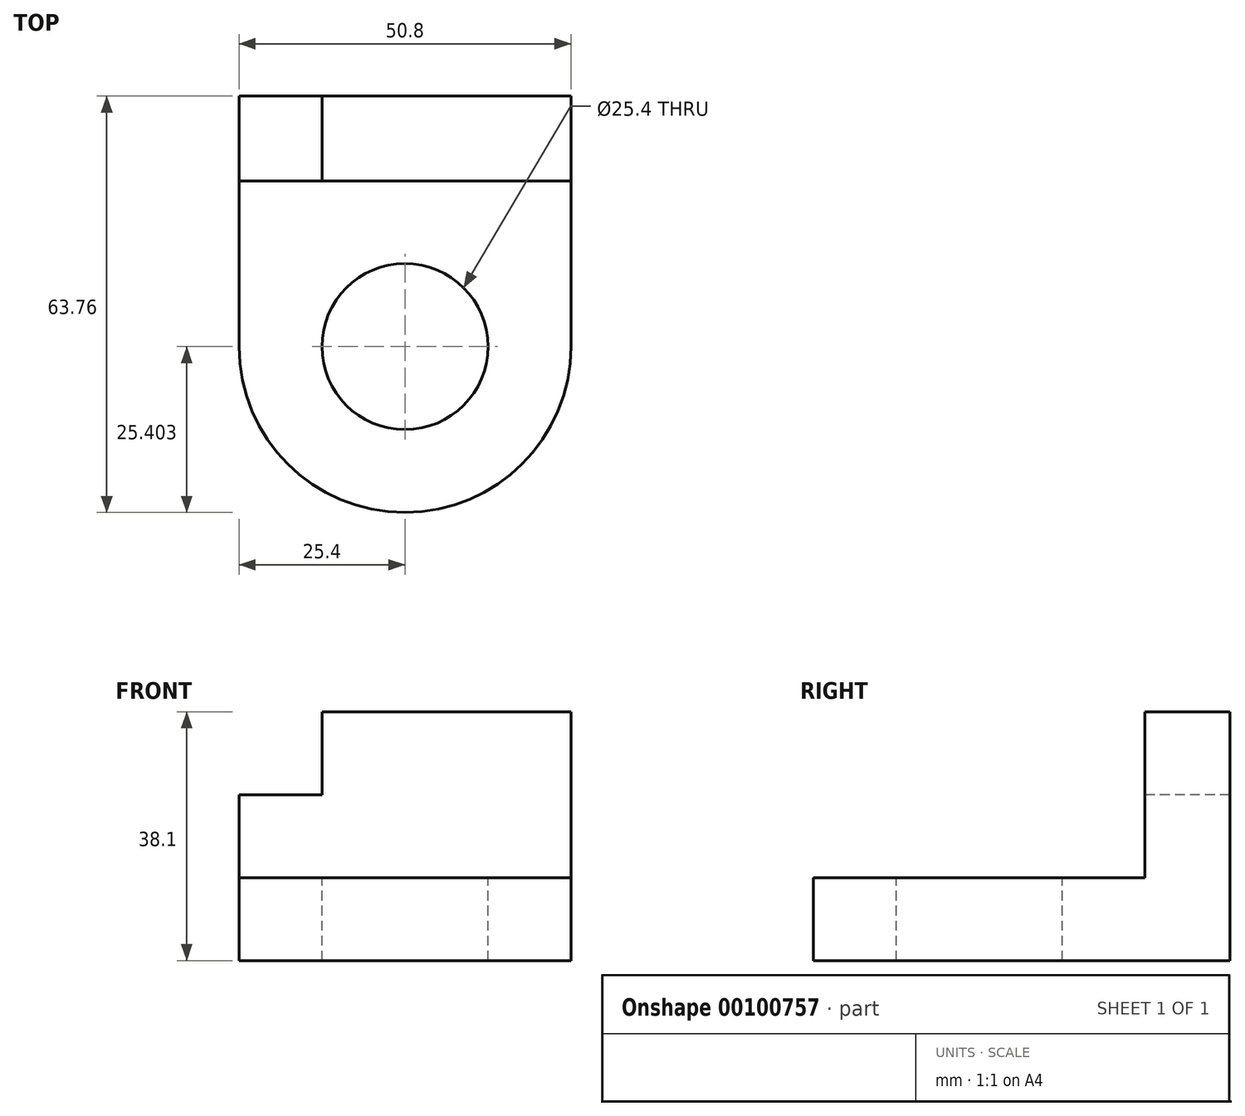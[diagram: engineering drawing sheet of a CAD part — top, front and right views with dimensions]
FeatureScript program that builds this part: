
annotation { "Feature Type Name" : "Feature", "Feature Type Description" : "" }
export const myFeature = defineFeature(function(context is Context, id is Id, definition is map)
    precondition{}
    {
        {
            var Q0;
            Q0=qCreatedBy(makeId("Top.planeOp"),FACE);
            var sketch = newSketch(context, id + "F0", { "sketchPlane" : qUnion([Q0])});
            skLineSegment(sketch, "E0.bottom", {"start": v(-25.4, 31.88) * mm, "end": v(25.4, 31.88) * mm});
            skLineSegment(sketch, "E0.top", {"start": v(-25.4, -31.88) * mm, "end": v(25.4, -31.88) * mm});
            skLineSegment(sketch, "E0.left", {"start": v(-25.4, 31.88) * mm, "end": v(-25.4, -31.88) * mm});
            skLineSegment(sketch, "E0.right", {"start": v(25.4, 31.88) * mm, "end": v(25.4, -31.88) * mm});
            skPoint(sketch, "E0.middle", {"position": v(0, 0) * mm});
            skSolve(sketch);
        }
        {
            var Q0;
            Q0=makeQuery(id+"F0.imprint","IMPRINT",FACE,{"disambiguationData":[TD([[makeQuery(id+"F0.imprint","IMPRINT",EDGE,{"derivedFrom":sQuery(id+"F0.wireOp",EDGE,"E0.bottom")}),-1.0]])]});
            extrude(context, id + "F1", {"entities" : qUnion([Q0]), "depth" : 12.7 * mm});
        }
        {
            var Q0;
            Q0=qCreatedBy(makeId("Top.planeOp"),FACE);
            var sketch = newSketch(context, id + "F2", { "sketchPlane" : qUnion([Q0])});
            skLineSegment(sketch, "E1.bottom", {"start": v(-25.4, 31.88) * mm, "end": v(25.4, 31.88) * mm});
            skLineSegment(sketch, "E1.top", {"start": v(-25.4, 18.85) * mm, "end": v(25.4, 18.85) * mm});
            skLineSegment(sketch, "E1.left", {"start": v(-25.4, 31.88) * mm, "end": v(-25.4, 18.85) * mm});
            skLineSegment(sketch, "E1.right", {"start": v(25.4, 31.88) * mm, "end": v(25.4, 18.85) * mm});
            skSolve(sketch);
        }
        {
            var Q0;
            Q0 = qSketchRegion(id + "F2", true);
            extrude(context, id + "F3", {"entities" : qUnion([Q0]), "operationType" : NewBodyOperationType.ADD, "depth" : 38.1 * mm});
        }
        {
            var Q0;
            Q0=makeQuery(id+"F3.opExtrude","CAP_FACE",FACE,{"disambiguationData":[OSD([sQuery(id+"F2.wireOp",EDGE,"E1.bottom"),sQuery(id+"F2.wireOp",EDGE,"E1.top"),sQuery(id+"F2.wireOp",EDGE,"E1.left"),sQuery(id+"F2.wireOp",EDGE,"E1.right")])],"isStart":false});
            var sketch = newSketch(context, id + "F4", { "sketchPlane" : qUnion([Q0])});
            skLineSegment(sketch, "E2.bottom", {"start": v(-25.4, 31.88) * mm, "end": v(-12.7, 31.88) * mm});
            skLineSegment(sketch, "E2.top", {"start": v(-25.4, 18.85) * mm, "end": v(-12.7, 18.85) * mm});
            skLineSegment(sketch, "E2.left", {"start": v(-25.4, 31.88) * mm, "end": v(-25.4, 18.85) * mm});
            skLineSegment(sketch, "E2.right", {"start": v(-12.7, 31.88) * mm, "end": v(-12.7, 18.85) * mm});
            skSolve(sketch);
        }
        {
            var Q0;
            Q0 = qSketchRegion(id + "F4", true);
            extrude(context, id + "F5", {"entities" : qUnion([Q0]), "operationType" : NewBodyOperationType.REMOVE, "oppositeDirection" : true, "depth" : 12.7 * mm});
        }
        {
            var Q0;
            Q0=makeQuery(id+"F1.opExtrude","SWEPT_EDGE",EDGE,{"disambiguationData":[OSD([sQuery(id+"F0.wireOp",EDGE,"E0.top"),sQuery(id+"F0.wireOp",EDGE,"E0.left")])]});
            var Q1;
            Q1=makeQuery(id+"F1.opExtrude","SWEPT_EDGE",EDGE,{"disambiguationData":[OSD([sQuery(id+"F0.wireOp",EDGE,"E0.top"),sQuery(id+"F0.wireOp",EDGE,"E0.right")])]});
            fillet(context, id + "F6", {"entities" : qUnion([Q0, Q1]), "radius" : 25.4 * mm, "tangentPropagation" : true, "allowEdgeOverflow" : false});
        }
        {
            var Q0;
            Q0=makeQuery(id+"F1.opExtrude","CAP_FACE",FACE,{"disambiguationData":[OSD([sQuery(id+"F0.wireOp",EDGE,"E0.bottom"),sQuery(id+"F0.wireOp",EDGE,"E0.top"),sQuery(id+"F0.wireOp",EDGE,"E0.left"),sQuery(id+"F0.wireOp",EDGE,"E0.right")])],"isStart":false});
            var sketch = newSketch(context, id + "F7", { "sketchPlane" : qUnion([Q0])});
            skCircle(sketch, "E3", {"center": v(0, -6.48) * mm, "radius": 12.7 * mm});
            skSolve(sketch);
        }
        {
            var Q0;
            Q0 = qSketchRegion(id + "F7", true);
            extrude(context, id + "F8", {"entities" : qUnion([Q0]), "operationType" : NewBodyOperationType.REMOVE, "endBound" : BoundingType.THROUGH_ALL, "oppositeDirection" : true, "depth" : 25.4 * mm});
        }
    });
